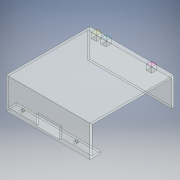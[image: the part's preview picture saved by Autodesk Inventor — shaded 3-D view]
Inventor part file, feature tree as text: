
AUTODESK INVENTOR PART (.ipt)
format: ipt  version: 2018 (Build 220112000, 112)  size: 185,344 bytes
history: native  units: in
note: dims shown in document units (in); Inventor stores cm internally (conversion verified against a paired STEP export)
features: extrude x4, sketch x4, fillet x1
ambient origin geometry x8: Origin, YZ Plane, XZ Plane, XY Plane, X Axis, Y Axis, Z Axis, Center Point
bodies: Solid1 (feature_tree)
feature tree (9):
  extrude  "Extrusion1"  Depth=2.126in
  extrude  "Extrusion2"  Depth=0.7874in
  extrude  "Extrusion3"  Depth=0.1575in
  fillet  "Fillet1"  Radius=0.1575in
  extrude  "Extrusion4"  Depth=0.1575in
  sketch  "Sketch1"  dims[d0=6.2992in d1=2.126in]
  sketch  "Sketch2"  dims[d2=2.3622in d3=0.7874in]
  sketch  "Sketch3"  dims[d4=0.1575in d5=0.1575in d6=0.1575in]
  sketch  "Sketch4"  dims[d7=0.1575in d8=0.1575in d9=0.1575in d10=6.2992in d11=0.0in d12=1.7717in d13=0.1575in d14=0.7874in d15=3.1496in d16=0.1969in d17=0.0in d18=0.1969in d19=2.2638in d20=1.1319in d21=1.1319in d22=0.7874in d23=0.5512in d24=0.1575in d25=0.5512in d26=0.2165in d27=0.1969in d28=0.0in d29=0.0787in d30=0.3937in d31=0.0in d32=0.3937in d33=0.3937in d34=0.3937in d35=0.3937in d36=0.3937in d37=0.3937in]
